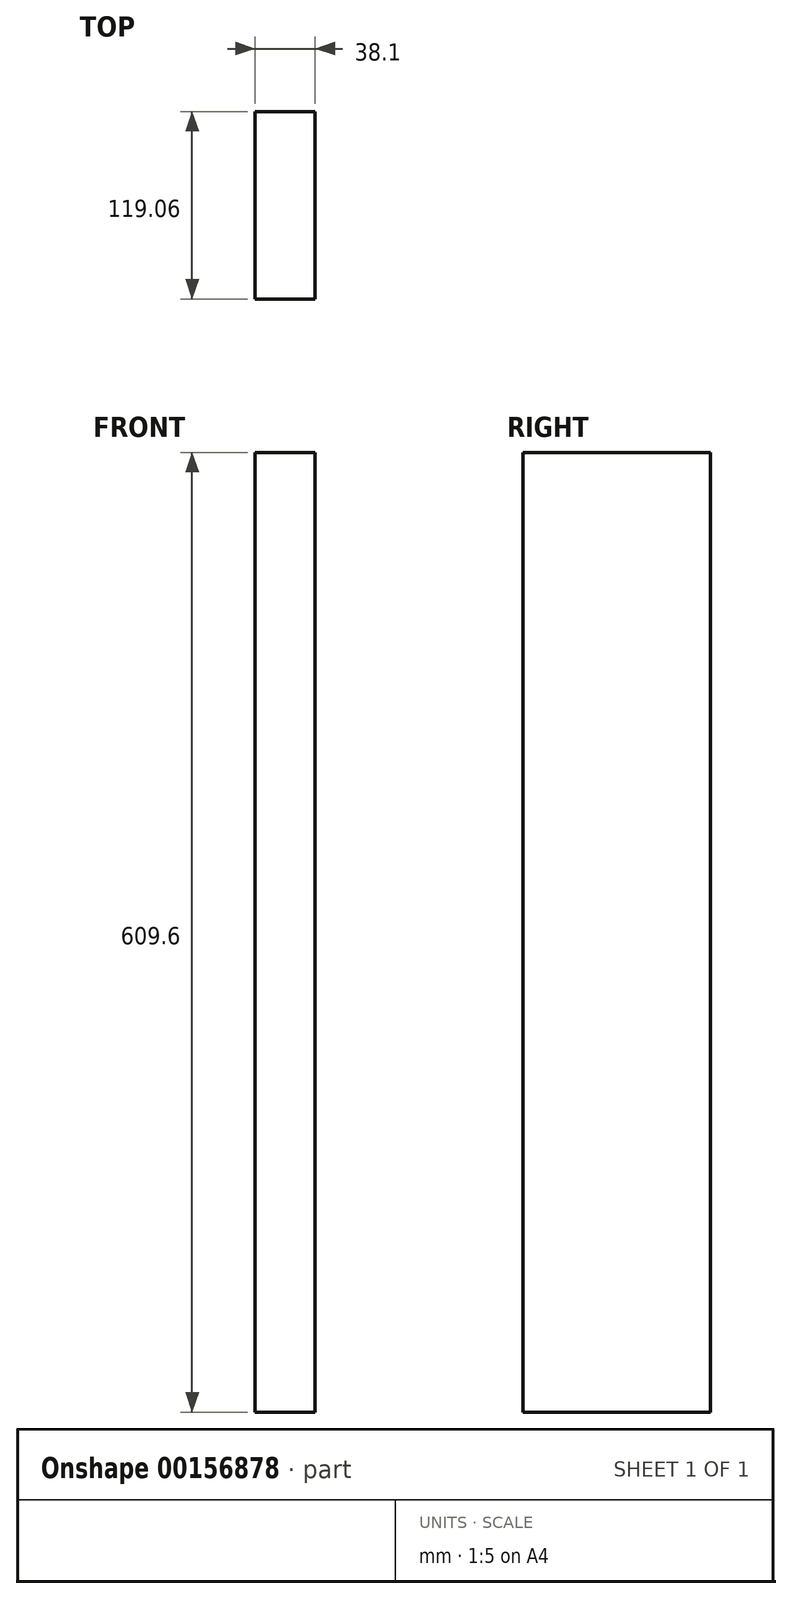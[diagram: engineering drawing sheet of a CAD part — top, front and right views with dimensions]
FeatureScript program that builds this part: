
annotation { "Feature Type Name" : "Feature", "Feature Type Description" : "" }
export const myFeature = defineFeature(function(context is Context, id is Id, definition is map)
    precondition{}
    {
        {
            var Q0;
            Q0=qCreatedBy(makeId("Front.planeOp"),FACE);
            var sketch = newSketch(context, id + "F0", { "sketchPlane" : qUnion([Q0])});
            skLineSegment(sketch, "E0.bottom", {"start": v(0, 0) * mm, "end": v(38.1, 0) * mm});
            skLineSegment(sketch, "E0.top", {"start": v(0, 609.6) * mm, "end": v(38.1, 609.6) * mm});
            skLineSegment(sketch, "E0.left", {"start": v(0, 0) * mm, "end": v(0, 609.6) * mm});
            skLineSegment(sketch, "E0.right", {"start": v(38.1, 0) * mm, "end": v(38.1, 609.6) * mm});
            skSolve(sketch);
        }
        {
            var Q0;
            Q0=makeQuery(id+"F0.imprint","IMPRINT",FACE,{"disambiguationData":[TD([[makeQuery(id+"F0.imprint","IMPRINT",EDGE,{"derivedFrom":sQuery(id+"F0.wireOp",EDGE,"E0.bottom")}),1.0]])]});
            extrude(context, id + "F1", {"entities" : qUnion([Q0]), "depth" : 119.06 * mm});
        }
    });
